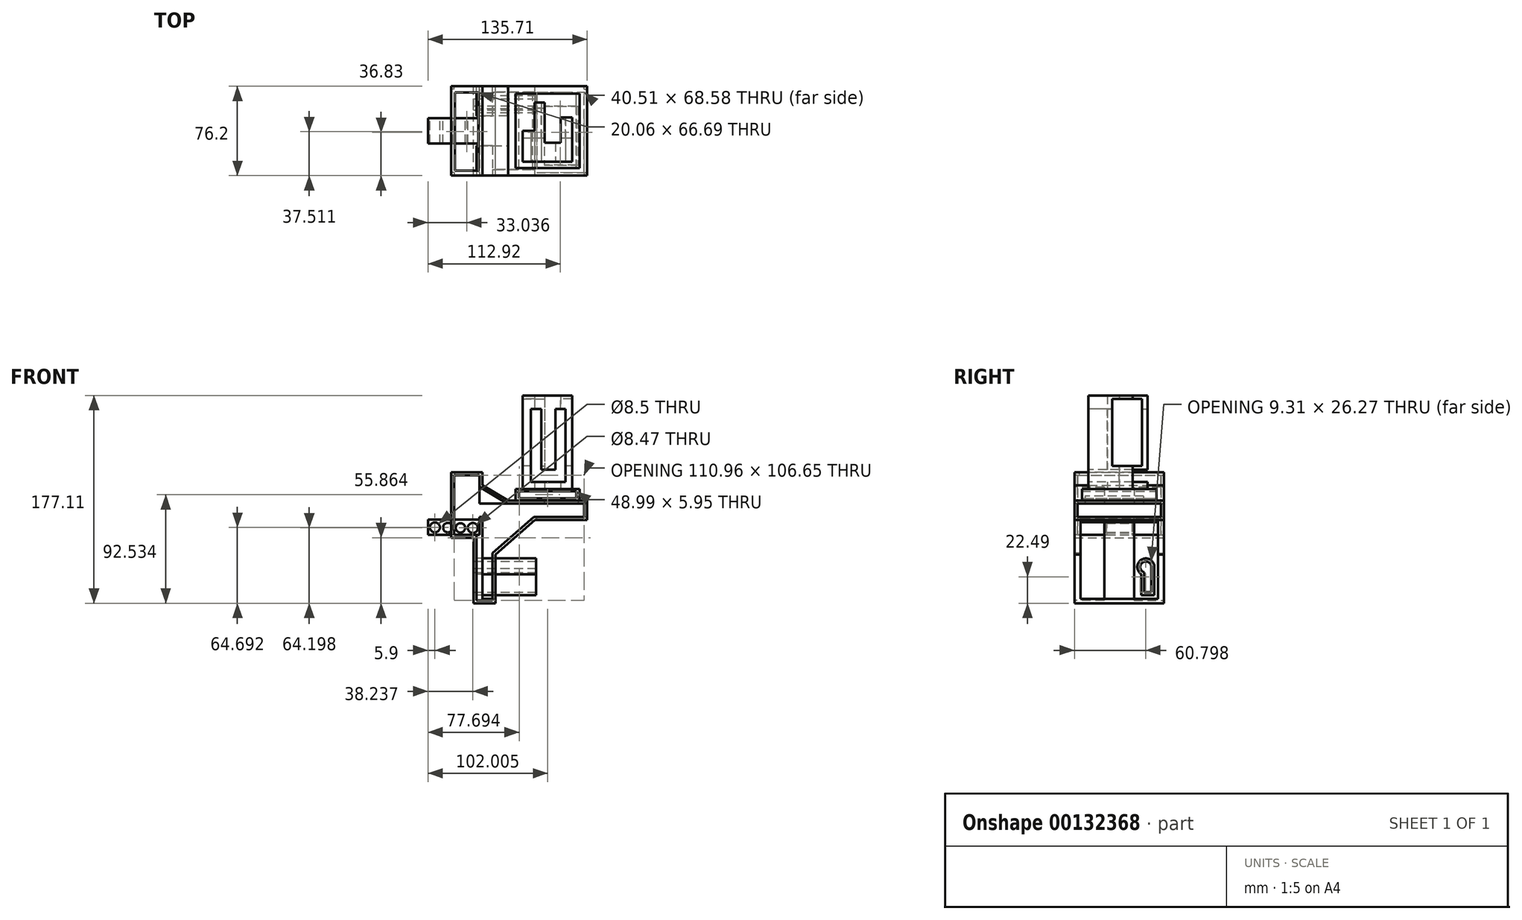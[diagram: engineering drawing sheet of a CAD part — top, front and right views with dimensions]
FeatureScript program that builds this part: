
annotation { "Feature Type Name" : "Feature", "Feature Type Description" : "" }
export const myFeature = defineFeature(function(context is Context, id is Id, definition is map)
    precondition{}
    {
        {
            var Q0;
            Q0=qCreatedBy(makeId("Front.planeOp"),FACE);
            var sketch = newSketch(context, id + "F0", { "sketchPlane" : qUnion([Q0])});
            skLineSegment(sketch, "E0", {"start": v(-48.79, 56.1) * mm, "end": v(-48.79, 0) * mm});
            skLineSegment(sketch, "E1", {"start": v(-48.79, 0) * mm, "end": v(-29.52, 0) * mm});
            skLineSegment(sketch, "E2", {"start": v(-29.52, 0) * mm, "end": v(-29.52, -55.64) * mm});
            skLineSegment(sketch, "E3", {"start": v(-29.52, -55.64) * mm, "end": v(-11, -55.64) * mm});
            skLineSegment(sketch, "E4", {"start": v(-11, -55.64) * mm, "end": v(-11, -14.17) * mm});
            skLineSegment(sketch, "E5", {"start": v(-11, -14.17) * mm, "end": v(22.62, 15.23) * mm});
            skLineSegment(sketch, "E6", {"start": v(22.62, 15.23) * mm, "end": v(67.25, 15.23) * mm});
            skLineSegment(sketch, "E7", {"start": v(67.25, 15.23) * mm, "end": v(67.25, 31.82) * mm});
            skLineSegment(sketch, "E8", {"start": v(67.25, 31.82) * mm, "end": v(0, 31.82) * mm});
            skLineSegment(sketch, "E9", {"start": v(0, 31.82) * mm, "end": v(-22.17, 44.94) * mm});
            skLineSegment(sketch, "E10", {"start": v(-22.17, 44.94) * mm, "end": v(-22.17, 56.1) * mm});
            skLineSegment(sketch, "E11", {"start": v(-22.17, 56.1) * mm, "end": v(-48.79, 56.1) * mm});
            skSolve(sketch);
        }
        {
            var Q0;
            Q0 = qSketchRegion(id + "F0", true);
            extrude(context, id + "F1", {"entities" : qUnion([Q0]), "endBound" : BoundingType.SYMMETRIC, "depth" : 76.2 * mm});
        }
        {
            var Q0;
            Q0=makeQuery(id+"F1.opExtrude","CAP_FACE",FACE,{"disambiguationData":[OSD([sQuery(id+"F0.wireOp",EDGE,"E0"),sQuery(id+"F0.wireOp",EDGE,"E1"),sQuery(id+"F0.wireOp",EDGE,"E2"),sQuery(id+"F0.wireOp",EDGE,"E3"),sQuery(id+"F0.wireOp",EDGE,"E4"),sQuery(id+"F0.wireOp",EDGE,"E5"),sQuery(id+"F0.wireOp",EDGE,"E6"),sQuery(id+"F0.wireOp",EDGE,"E7"),sQuery(id+"F0.wireOp",EDGE,"E8"),sQuery(id+"F0.wireOp",EDGE,"E9"),sQuery(id+"F0.wireOp",EDGE,"E10"),sQuery(id+"F0.wireOp",EDGE,"E11")])],"isStart":false});
            var sketch = newSketch(context, id + "F2", { "sketchPlane" : qUnion([Q0])});
            skLineSegment(sketch, "E12.0", {"start": v(64.71, 29.28) * mm, "end": v(-0.7, 29.28) * mm});
            skLineSegment(sketch, "E12.1", {"start": v(-46.25, 2.54) * mm, "end": v(-26.98, 2.54) * mm});
            skLineSegment(sketch, "E12.2", {"start": v(-46.25, 53.55) * mm, "end": v(-46.25, 2.54) * mm});
            skLineSegment(sketch, "E12.3", {"start": v(-24.7, 53.55) * mm, "end": v(-46.25, 53.55) * mm});
            skLineSegment(sketch, "E12.4", {"start": v(-24.7, 43.49) * mm, "end": v(-24.7, 53.55) * mm});
            skLineSegment(sketch, "E12.5", {"start": v(-26.98, 2.54) * mm, "end": v(-26.98, -53.1) * mm});
            skLineSegment(sketch, "E12.6", {"start": v(-0.7, 29.28) * mm, "end": v(-24.7, 43.49) * mm});
            skLineSegment(sketch, "E12.7", {"start": v(-26.98, -53.1) * mm, "end": v(-13.55, -53.1) * mm});
            skLineSegment(sketch, "E12.8", {"start": v(-13.55, -53.1) * mm, "end": v(-13.55, -13.02) * mm});
            skLineSegment(sketch, "E12.9", {"start": v(-13.55, -13.02) * mm, "end": v(21.67, 17.77) * mm});
            skLineSegment(sketch, "E12.10", {"start": v(21.67, 17.77) * mm, "end": v(64.71, 17.77) * mm});
            skLineSegment(sketch, "E12.11", {"start": v(64.71, 17.77) * mm, "end": v(64.71, 29.28) * mm});
            skSolve(sketch);
        }
        {
            var Q0;
            Q0 = qSketchRegion(id + "F2", true);
            extrude(context, id + "F3", {"entities" : qUnion([Q0]), "operationType" : NewBodyOperationType.REMOVE, "oppositeDirection" : true, "depth" : 25.4 * mm});
        }
        {
            var Q0;
            Q0=makeQuery(id+"F1.opExtrude","SWEPT_FACE",FACE,{"disambiguationData":[OSD([sQuery(id+"F0.wireOp",EDGE,"E7")])]});
            var sketch = newSketch(context, id + "F4", { "sketchPlane" : qUnion([Q0])});
            skLineSegment(sketch, "E13.0", {"start": v(-35.56, 17.77) * mm, "end": v(-35.56, 29.28) * mm});
            skLineSegment(sketch, "E13.1", {"start": v(-35.56, 17.77) * mm, "end": v(35.56, 17.77) * mm});
            skLineSegment(sketch, "E13.2", {"start": v(35.56, 17.77) * mm, "end": v(35.56, 29.28) * mm});
            skLineSegment(sketch, "E13.3", {"start": v(-35.56, 29.28) * mm, "end": v(35.56, 29.28) * mm});
            skSolve(sketch);
        }
        {
            var Q0;
            Q0 = qSketchRegion(id + "F4", true);
            extrude(context, id + "F5", {"entities" : qUnion([Q0]), "operationType" : NewBodyOperationType.REMOVE, "oppositeDirection" : true, "depth" : 166.56 * mm});
        }
        {
            var Q0;
            Q0=makeQuery(id+"F1.opExtrude","SWEPT_FACE",FACE,{"disambiguationData":[OSD([sQuery(id+"F0.wireOp",EDGE,"E0")])]});
            var sketch = newSketch(context, id + "F6", { "sketchPlane" : qUnion([Q0])});
            skLineSegment(sketch, "E14.0", {"start": v(35.56, 53.55) * mm, "end": v(-35.56, 53.55) * mm});
            skLineSegment(sketch, "E14.1", {"start": v(35.56, 53.55) * mm, "end": v(35.56, 2.54) * mm});
            skLineSegment(sketch, "E14.2", {"start": v(35.56, 2.54) * mm, "end": v(-35.56, 2.54) * mm});
            skLineSegment(sketch, "E14.3", {"start": v(-35.56, 53.55) * mm, "end": v(-35.56, 2.54) * mm});
            skSolve(sketch);
        }
        {
            var Q0;
            Q0 = qSketchRegion(id + "F6", true);
            extrude(context, id + "F7", {"entities" : qUnion([Q0]), "operationType" : NewBodyOperationType.REMOVE, "oppositeDirection" : true, "depth" : 24.13 * mm});
        }
        {
            var Q0;
            Q0=makeQuery(id+"F5.boolean.opBoolean","MERGE",FACE,{"derivedFrom":[makeQuery(id+"F3.boolean.opBoolean","COPY",FACE,{"derivedFrom":makeQuery(id+"F3.opExtrude","SWEPT_FACE",FACE,{"disambiguationData":[OSD([sQuery(id+"F2.wireOp",EDGE,"E12.10")])]})}),makeQuery(id+"F5.opExtrude","SWEPT_FACE",FACE,{"disambiguationData":[OSD([sQuery(id+"F4.wireOp",EDGE,"E13.1")])]})]});
            var sketch = newSketch(context, id + "F8", { "sketchPlane" : qUnion([Q0])});
            skLineSegment(sketch, "E15.0", {"start": v(24.2, -33.02) * mm, "end": v(24.2, -35.56) * mm});
            skLineSegment(sketch, "E15.1", {"start": v(64.71, -35.56) * mm, "end": v(64.71, 33.02) * mm});
            skLineSegment(sketch, "E15.2", {"start": v(-22.12, 33.02) * mm, "end": v(64.71, 33.02) * mm});
            skLineSegment(sketch, "E15.3", {"start": v(24.2, -35.56) * mm, "end": v(64.71, -35.56) * mm});
            skLineSegment(sketch, "E15.4", {"start": v(-22.12, -33.02) * mm, "end": v(-22.12, 33.02) * mm});
            skLineSegment(sketch, "E15.5", {"start": v(-22.12, -33.02) * mm, "end": v(24.2, -33.02) * mm});
            skSolve(sketch);
        }
        {
            var Q0;
            Q0 = qSketchRegion(id + "F8", true);
            extrude(context, id + "F9", {"entities" : qUnion([Q0]), "operationType" : NewBodyOperationType.REMOVE, "oppositeDirection" : true, "depth" : 69.85 * mm});
        }
        {
            var Q0;
            Q0=makeQuery(id+"F1.opExtrude","CAP_FACE",FACE,{"disambiguationData":[OSD([sQuery(id+"F0.wireOp",EDGE,"E0"),sQuery(id+"F0.wireOp",EDGE,"E1"),sQuery(id+"F0.wireOp",EDGE,"E2"),sQuery(id+"F0.wireOp",EDGE,"E3"),sQuery(id+"F0.wireOp",EDGE,"E4"),sQuery(id+"F0.wireOp",EDGE,"E5"),sQuery(id+"F0.wireOp",EDGE,"E6"),sQuery(id+"F0.wireOp",EDGE,"E7"),sQuery(id+"F0.wireOp",EDGE,"E8"),sQuery(id+"F0.wireOp",EDGE,"E9"),sQuery(id+"F0.wireOp",EDGE,"E10"),sQuery(id+"F0.wireOp",EDGE,"E11")])],"isStart":true});
            var sketch = newSketch(context, id + "F10", { "sketchPlane" : qUnion([Q0])});
            skLineSegment(sketch, "E16.0", {"start": v(-21.67, 17.77) * mm, "end": v(-64.71, 17.77) * mm});
            skLineSegment(sketch, "E16.1", {"start": v(24.7, 53.55) * mm, "end": v(46.25, 53.55) * mm});
            skLineSegment(sketch, "E16.2", {"start": v(24.7, 43.49) * mm, "end": v(24.7, 53.55) * mm});
            skLineSegment(sketch, "E16.3", {"start": v(0.7, 29.28) * mm, "end": v(24.7, 43.49) * mm});
            skLineSegment(sketch, "E16.4", {"start": v(-64.71, 29.28) * mm, "end": v(0.7, 29.28) * mm});
            skLineSegment(sketch, "E16.5", {"start": v(46.25, 53.55) * mm, "end": v(46.25, 2.54) * mm});
            skLineSegment(sketch, "E16.6", {"start": v(-64.71, 17.77) * mm, "end": v(-64.71, 29.28) * mm});
            skLineSegment(sketch, "E16.7", {"start": v(46.25, 2.54) * mm, "end": v(26.98, 2.54) * mm});
            skLineSegment(sketch, "E16.8", {"start": v(26.98, 2.54) * mm, "end": v(26.98, -53.1) * mm});
            skLineSegment(sketch, "E16.9", {"start": v(26.98, -53.1) * mm, "end": v(13.55, -53.1) * mm});
            skLineSegment(sketch, "E16.10", {"start": v(13.55, -53.1) * mm, "end": v(13.55, -13.02) * mm});
            skLineSegment(sketch, "E16.11", {"start": v(13.55, -13.02) * mm, "end": v(-21.67, 17.77) * mm});
            skSolve(sketch);
        }
        {
            var Q0;
            Q0=makeQuery(id+"F10.imprint","IMPRINT",FACE,{"disambiguationData":[TD([[makeQuery(id+"F10.imprint","IMPRINT",EDGE,{"derivedFrom":sQuery(id+"F10.wireOp",EDGE,"E16.0")}),-1.0]])]});
            extrude(context, id + "F11", {"entities" : qUnion([Q0]), "operationType" : NewBodyOperationType.REMOVE, "oppositeDirection" : true, "depth" : 25.4 * mm});
        }
        {
            var Q0;
            Q0=makeQuery(id+"F9.boolean.opBoolean","COPY",FACE,{"derivedFrom":makeQuery(id+"F9.opExtrude","SWEPT_FACE",FACE,{"disambiguationData":[OSD([sQuery(id+"F8.wireOp",EDGE,"E15.5")])]})});
            var sketch = newSketch(context, id + "F12", { "sketchPlane" : qUnion([Q0])});
            skLineSegment(sketch, "E17", {"start": v(-24.2, 17.77) * mm, "end": v(-24.2, 15.23) * mm});
            skLineSegment(sketch, "E18", {"start": v(-24.2, 15.23) * mm, "end": v(-22.55, 15.22) * mm});
            skLineSegment(sketch, "E19", {"start": v(-22.55, 15.22) * mm, "end": v(-20.49, 13.37) * mm});
            skLineSegment(sketch, "E20", {"start": v(-20.49, 13.37) * mm, "end": v(-20.49, 16.74) * mm});
            skLineSegment(sketch, "E21", {"start": v(-20.49, 16.74) * mm, "end": v(-21.67, 17.77) * mm});
            skSolve(sketch);
        }
        {
            var Q0;
            Q0 = qSketchRegion(id + "F12", true);
            var Q1;
            Q1=makeQuery(id+"F12.imprint","IMPRINT",FACE,{"disambiguationData":[TD([[makeQuery(id+"F12.imprint","IMPRINT",EDGE,{"derivedFrom":sQuery(id+"F12.wireOp",EDGE,"E17")}),-1.0]])]});
            extrude(context, id + "F13", {"entities" : qUnion([Q0, Q1]), "operationType" : NewBodyOperationType.ADD, "depth" : 70 * mm});
        }
        {
            var Q0;
            Q0=makeQuery(id+"F1.opExtrude","SWEPT_FACE",FACE,{"disambiguationData":[OSD([sQuery(id+"F0.wireOp",EDGE,"E8")])]});
            var sketch = newSketch(context, id + "F14", { "sketchPlane" : qUnion([Q0])});
            skLineSegment(sketch, "E22.0", {"start": v(60.9, -31.75) * mm, "end": v(6.35, -31.75) * mm});
            skLineSegment(sketch, "E22.1", {"start": v(60.9, -31.75) * mm, "end": v(60.9, 31.75) * mm});
            skLineSegment(sketch, "E22.2", {"start": v(60.9, 31.75) * mm, "end": v(6.35, 31.75) * mm});
            skLineSegment(sketch, "E22.3", {"start": v(6.35, -31.75) * mm, "end": v(6.35, 31.75) * mm});
            skSolve(sketch);
        }
        {
            var Q0;
            Q0 = qSketchRegion(id + "F14", true);
            extrude(context, id + "F15", {"entities" : qUnion([Q0]), "operationType" : NewBodyOperationType.ADD, "depth" : 9.97 * mm});
        }
        {
            var Q0;
            Q0=makeQuery(id+"F15.opExtrude","CAP_FACE",FACE,{"disambiguationData":[OSD([sQuery(id+"F14.wireOp",EDGE,"E22.0"),sQuery(id+"F14.wireOp",EDGE,"E22.1"),sQuery(id+"F14.wireOp",EDGE,"E22.2"),sQuery(id+"F14.wireOp",EDGE,"E22.3")])],"isStart":false});
            var sketch = newSketch(context, id + "F16", { "sketchPlane" : qUnion([Q0])});
            skLineSegment(sketch, "E23", {"start": v(54.4, -26.19) * mm, "end": v(12.17, -26.19) * mm});
            skLineSegment(sketch, "E24", {"start": v(12.17, -26.19) * mm, "end": v(12.17, 0) * mm});
            skLineSegment(sketch, "E25", {"start": v(12.17, 0) * mm, "end": v(22.28, 0) * mm});
            skLineSegment(sketch, "E26", {"start": v(22.28, 0) * mm, "end": v(22.28, 24.14) * mm});
            skLineSegment(sketch, "E27", {"start": v(22.28, 24.14) * mm, "end": v(30.93, 24.14) * mm});
            skLineSegment(sketch, "E28", {"start": v(30.93, 24.14) * mm, "end": v(30.93, -10.16) * mm});
            skLineSegment(sketch, "E29", {"start": v(30.93, -10.16) * mm, "end": v(44.72, -10.16) * mm});
            skLineSegment(sketch, "E30", {"start": v(44.72, -10.16) * mm, "end": v(44.72, 11.64) * mm});
            skLineSegment(sketch, "E31", {"start": v(44.72, 11.64) * mm, "end": v(54.4, 11.64) * mm});
            skLineSegment(sketch, "E32", {"start": v(54.4, 11.64) * mm, "end": v(54.4, -26.19) * mm});
            skSolve(sketch);
        }
        {
            var Q0;
            Q0 = qSketchRegion(id + "F16", true);
            extrude(context, id + "F17", {"entities" : qUnion([Q0]), "operationType" : NewBodyOperationType.ADD, "depth" : 79.68 * mm});
        }
        {
            var Q0;
            Q0=makeQuery(id+"F17.opExtrude","SWEPT_FACE",FACE,{"disambiguationData":[OSD([sQuery(id+"F16.wireOp",EDGE,"E23")])]});
            var sketch = newSketch(context, id + "F18", { "sketchPlane" : qUnion([Q0])});
            skLineSegment(sketch, "E33", {"start": v(19.37, 109.94) * mm, "end": v(19.37, 47.68) * mm});
            skLineSegment(sketch, "E34", {"start": v(19.37, 47.68) * mm, "end": v(48.9, 47.68) * mm});
            skLineSegment(sketch, "E35", {"start": v(48.9, 47.68) * mm, "end": v(48.9, 109.94) * mm});
            skLineSegment(sketch, "E36", {"start": v(48.9, 109.94) * mm, "end": v(40.25, 109.94) * mm});
            skLineSegment(sketch, "E37", {"start": v(40.25, 109.94) * mm, "end": v(40.25, 58.17) * mm});
            skLineSegment(sketch, "E38", {"start": v(40.25, 58.17) * mm, "end": v(27.98, 58.17) * mm});
            skLineSegment(sketch, "E39", {"start": v(27.98, 58.17) * mm, "end": v(27.98, 109.94) * mm});
            skLineSegment(sketch, "E40", {"start": v(27.98, 109.94) * mm, "end": v(19.37, 109.94) * mm});
            skSolve(sketch);
        }
        {
            var Q0;
            Q0 = qSketchRegion(id + "F18", true);
            extrude(context, id + "F19", {"entities" : qUnion([Q0]), "operationType" : NewBodyOperationType.REMOVE, "oppositeDirection" : true, "depth" : 169.27 * mm});
        }
        {
            var Q0;
            {var subQ1=sQuery(id+"F16.wireOp",EDGE,"E28");Q0=makeQuery(id+"F19.boolean.opBoolean","SPLIT",FACE,{"disambiguationData":[TD([makeQuery(id+"F19.opExtrude","SWEPT_FACE",FACE,{"disambiguationData":[OSD([sQuery(id+"F18.wireOp",EDGE,"E38")])]})])],"derivedFrom":makeQuery(id+"F17.opExtrude","SWEPT_FACE",FACE,{"disambiguationData":[OSD([subQ1])]})});}
            var sketch = newSketch(context, id + "F20", { "sketchPlane" : qUnion([Q0])});
            skLineSegment(sketch, "E41", {"start": v(-6.04, 118.71) * mm, "end": v(-6.04, 61.56) * mm});
            skLineSegment(sketch, "E42", {"start": v(-6.04, 61.56) * mm, "end": v(19.5, 61.56) * mm});
            skLineSegment(sketch, "E43", {"start": v(19.5, 61.56) * mm, "end": v(19.5, 118.71) * mm});
            skLineSegment(sketch, "E44", {"start": v(-6.04, 118.71) * mm, "end": v(19.5, 118.71) * mm});
            skSolve(sketch);
        }
        {
            var Q0;
            Q0 = qSketchRegion(id + "F20", true);
            extrude(context, id + "F21", {"entities" : qUnion([Q0]), "operationType" : NewBodyOperationType.REMOVE, "endBound" : BoundingType.THROUGH_ALL, "oppositeDirection" : true, "depth" : 25.4 * mm, "hasSecondDirection" : true, "secondDirectionOppositeDirection" : false, "secondDirectionDepth" : 25.4 * mm});
        }
        {
            var Q0;
            Q0=makeQuery(id+"F11.boolean.opBoolean","MERGE",FACE,{"derivedFrom":[makeQuery(id+"F5.boolean.opBoolean","MERGE",FACE,{"derivedFrom":[makeQuery(id+"F3.boolean.opBoolean","COPY",FACE,{"derivedFrom":makeQuery(id+"F3.opExtrude","SWEPT_FACE",FACE,{"disambiguationData":[OSD([sQuery(id+"F2.wireOp",EDGE,"E12.0")])]})}),makeQuery(id+"F5.opExtrude","SWEPT_FACE",FACE,{"disambiguationData":[OSD([sQuery(id+"F4.wireOp",EDGE,"E13.3")])]})]}),makeQuery(id+"F11.opExtrude","SWEPT_FACE",FACE,{"disambiguationData":[OSD([sQuery(id+"F10.wireOp",EDGE,"E16.4")])]})]});
            var sketch = newSketch(context, id + "F22", { "sketchPlane" : qUnion([Q0])});
            skLineSegment(sketch, "E45.bottom", {"start": v(30.6, -20.9) * mm, "end": v(59.4, -20.9) * mm});
            skLineSegment(sketch, "E45.top", {"start": v(30.6, 29.1) * mm, "end": v(59.4, 29.1) * mm});
            skLineSegment(sketch, "E45.left", {"start": v(30.6, -20.9) * mm, "end": v(30.6, 29.1) * mm});
            skLineSegment(sketch, "E45.right", {"start": v(59.4, -20.9) * mm, "end": v(59.4, 29.1) * mm});
            skSolve(sketch);
        }
        {
            var Q0;
            Q0 = qSketchRegion(id + "F22", true);
            extrude(context, id + "F23", {"entities" : qUnion([Q0]), "operationType" : NewBodyOperationType.REMOVE, "oppositeDirection" : true, "depth" : 6.35 * mm});
        }
        {
            var Q0;
            Q0=makeQuery(id+"F15.opExtrude","SWEPT_FACE",FACE,{"disambiguationData":[OSD([sQuery(id+"F14.wireOp",EDGE,"E22.2")])]});
            var sketch = newSketch(context, id + "F24", { "sketchPlane" : qUnion([Q0])});
            skLineSegment(sketch, "E46", {"start": v(-58.04, 39.87) * mm, "end": v(-58.04, 33.92) * mm});
            skLineSegment(sketch, "E47", {"start": v(-58.04, 33.92) * mm, "end": v(-9.05, 33.92) * mm});
            skLineSegment(sketch, "E48", {"start": v(-9.05, 33.92) * mm, "end": v(-9.05, 39.87) * mm});
            skLineSegment(sketch, "E49", {"start": v(-9.05, 39.87) * mm, "end": v(-58.04, 39.87) * mm});
            skSolve(sketch);
        }
        {
            var Q0;
            Q0 = qSketchRegion(id + "F24", true);
            extrude(context, id + "F25", {"entities" : qUnion([Q0]), "operationType" : NewBodyOperationType.REMOVE, "endBound" : BoundingType.THROUGH_ALL, "oppositeDirection" : true, "depth" : 25.4 * mm});
        }
        {
            var Q0;
            Q0=makeQuery(id+"F1.opExtrude","SWEPT_FACE",FACE,{"disambiguationData":[OSD([sQuery(id+"F0.wireOp",EDGE,"E11")])]});
            var sketch = newSketch(context, id + "F26", { "sketchPlane" : qUnion([Q0])});
            skLineSegment(sketch, "E50", {"start": v(-45.46, 32.76) * mm, "end": v(-45.46, -33.93) * mm});
            skLineSegment(sketch, "E51", {"start": v(-45.46, -33.93) * mm, "end": v(-25.4, -33.93) * mm});
            skLineSegment(sketch, "E52", {"start": v(-25.4, -33.93) * mm, "end": v(-25.4, 32.76) * mm});
            skLineSegment(sketch, "E53", {"start": v(-25.4, 32.76) * mm, "end": v(-45.46, 32.76) * mm});
            skSolve(sketch);
        }
        {
            var Q0;
            Q0=makeQuery(id+"F26.imprint","IMPRINT",FACE,{"disambiguationData":[TD([[makeQuery(id+"F26.imprint","IMPRINT",EDGE,{"derivedFrom":sQuery(id+"F26.wireOp",EDGE,"E50")}),1.0]])]});
            extrude(context, id + "F27", {"entities" : qUnion([Q0]), "operationType" : NewBodyOperationType.REMOVE, "oppositeDirection" : true, "depth" : 25.4 * mm});
        }
        {
            var Q0;
            Q0=makeQuery(id+"F11.boolean.opBoolean","COPY",FACE,{"derivedFrom":makeQuery(id+"F11.opExtrude","SWEPT_FACE",FACE,{"disambiguationData":[OSD([sQuery(id+"F10.wireOp",EDGE,"E16.8")])]})});
            var sketch = newSketch(context, id + "F28", { "sketchPlane" : qUnion([Q0])});
            skArc(sketch, "E54", {"start": v(29.9, -26.28) * mm, "mid": v(20, -18) * mm, "end": v(18.78, -30.84) * mm});
            skLineSegment(sketch, "E55", {"start": v(18.78, -30.84) * mm, "end": v(18.78, -48.82) * mm});
            skLineSegment(sketch, "E56", {"start": v(18.78, -48.82) * mm, "end": v(29.9, -48.82) * mm});
            skLineSegment(sketch, "E57", {"start": v(29.9, -48.82) * mm, "end": v(29.9, -26.28) * mm});
            skSolve(sketch);
        }
        {
            var Q0;
            Q0 = qSketchRegion(id + "F28", true);
            extrude(context, id + "F29", {"entities" : qUnion([Q0]), "operationType" : NewBodyOperationType.ADD, "depth" : 50.8 * mm});
        }
        {
            var Q0;
            Q0=makeQuery(id+"F29.opExtrude","CAP_FACE",FACE,{"disambiguationData":[OSD([sQuery(id+"F28.wireOp",EDGE,"E54"),sQuery(id+"F28.wireOp",EDGE,"E55"),sQuery(id+"F28.wireOp",EDGE,"E56"),sQuery(id+"F28.wireOp",EDGE,"E57")])],"isStart":false});
            var sketch = newSketch(context, id + "F30", { "sketchPlane" : qUnion([Q0])});
            skLineSegment(sketch, "E58.0", {"start": v(27.35, -46.28) * mm, "end": v(27.35, -25.98) * mm});
            skLineSegment(sketch, "E58.1", {"start": v(21.32, -46.28) * mm, "end": v(27.35, -46.28) * mm});
            skLineSegment(sketch, "E58.2", {"start": v(21.32, -29.26) * mm, "end": v(21.32, -46.28) * mm});
            skArc(sketch, "E58.3", {"start": v(27.35, -25.98) * mm, "mid": v(20.5, -20.58) * mm, "end": v(21.32, -29.26) * mm});
            skSolve(sketch);
        }
        {
            var Q0;
            Q0 = qSketchRegion(id + "F30", true);
            extrude(context, id + "F31", {"entities" : qUnion([Q0]), "operationType" : NewBodyOperationType.REMOVE, "oppositeDirection" : true, "depth" : 86.32 * mm});
        }
        {
            var Q0;
            {var subQ0=sQuery(id+"F2.wireOp",EDGE,"E12.1");var subQ2=sQuery(id+"F6.wireOp",EDGE,"E14.3");var subQ3=sQuery(id+"F6.wireOp",EDGE,"E14.2");Q0=makeQuery(id+"F7.boolean.opBoolean","COPY",FACE,{"disambiguationData":[TD([makeQuery(id+"F3.boolean.opBoolean","COPY",FACE,{"derivedFrom":makeQuery(id+"F3.opExtrude","SWEPT_FACE",FACE,{"disambiguationData":[OSD([subQ0])]})})])],"derivedFrom":makeQuery(id+"F7.opExtrude","CAP_FACE",FACE,{"disambiguationData":[OSD([sQuery(id+"F6.wireOp",EDGE,"E14.0"),sQuery(id+"F6.wireOp",EDGE,"E14.1"),subQ3,subQ2])],"isStart":false})});}
            var sketch = newSketch(context, id + "F32", { "sketchPlane" : qUnion([Q0])});
            skLineSegment(sketch, "E59.bottom", {"start": v(-10.86, 15.77) * mm, "end": v(10.68, 15.77) * mm});
            skLineSegment(sketch, "E59.top", {"start": v(-10.86, 2.54) * mm, "end": v(10.68, 2.54) * mm});
            skLineSegment(sketch, "E59.left", {"start": v(-10.86, 15.77) * mm, "end": v(-10.86, 2.54) * mm});
            skLineSegment(sketch, "E59.right", {"start": v(10.68, 15.77) * mm, "end": v(10.68, 2.54) * mm});
            skSolve(sketch);
        }
        {
            var Q0;
            Q0 = qSketchRegion(id + "F32", true);
            extrude(context, id + "F33", {"entities" : qUnion([Q0]), "operationType" : NewBodyOperationType.ADD, "depth" : 43.8 * mm});
        }
        {
            var Q0;
            Q0=makeQuery(id+"F33.opExtrude","SWEPT_FACE",FACE,{"disambiguationData":[OSD([sQuery(id+"F32.wireOp",EDGE,"E59.left")])]});
            var sketch = newSketch(context, id + "F34", { "sketchPlane" : qUnion([Q0])});
            skCircle(sketch, "E60", {"center": v(30.22, 8.56) * mm, "radius": 4.24 * mm});
            skCircle(sketch, "E61", {"center": v(40.78, 8.57) * mm, "radius": 4.02 * mm});
            skCircle(sketch, "E62", {"center": v(51.44, 8.84) * mm, "radius": 4.1 * mm});
            skCircle(sketch, "E63", {"center": v(62.56, 9.05) * mm, "radius": 4.25 * mm});
            skSolve(sketch);
        }
        {
            var Q0;
            Q0 = qSketchRegion(id + "F34", true);
            extrude(context, id + "F35", {"entities" : qUnion([Q0]), "operationType" : NewBodyOperationType.REMOVE, "oppositeDirection" : true, "depth" : 25.4 * mm});
        }
    });
